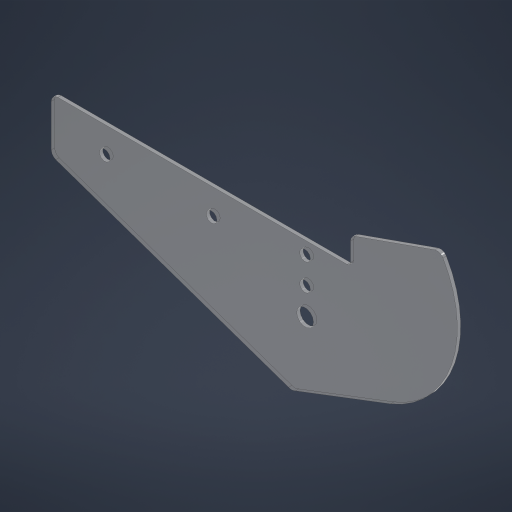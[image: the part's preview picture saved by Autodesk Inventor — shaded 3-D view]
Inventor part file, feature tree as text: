
AUTODESK INVENTOR PART (.ipt)
format: ipt  version: 2024 (Build 280153000, 153)  size: 219,136 bytes
history: native  units: in
note: dims shown in document units (in); Inventor stores cm internally (conversion verified against a paired STEP export)
features: extrude x1, sketch x1
ambient origin geometry x8: Origin, YZ Plane, XZ Plane, XY Plane, X Axis, Y Axis, Z Axis, Center Point
bodies: Solid1 (feature_tree)
feature tree (2):
  extrude  "Extrusion1"  Depth=0.125in
  sketch  "Sketch1"  dims[d0=0.0625in d1=0.0in d2=0.125in d3=0.0625in]
